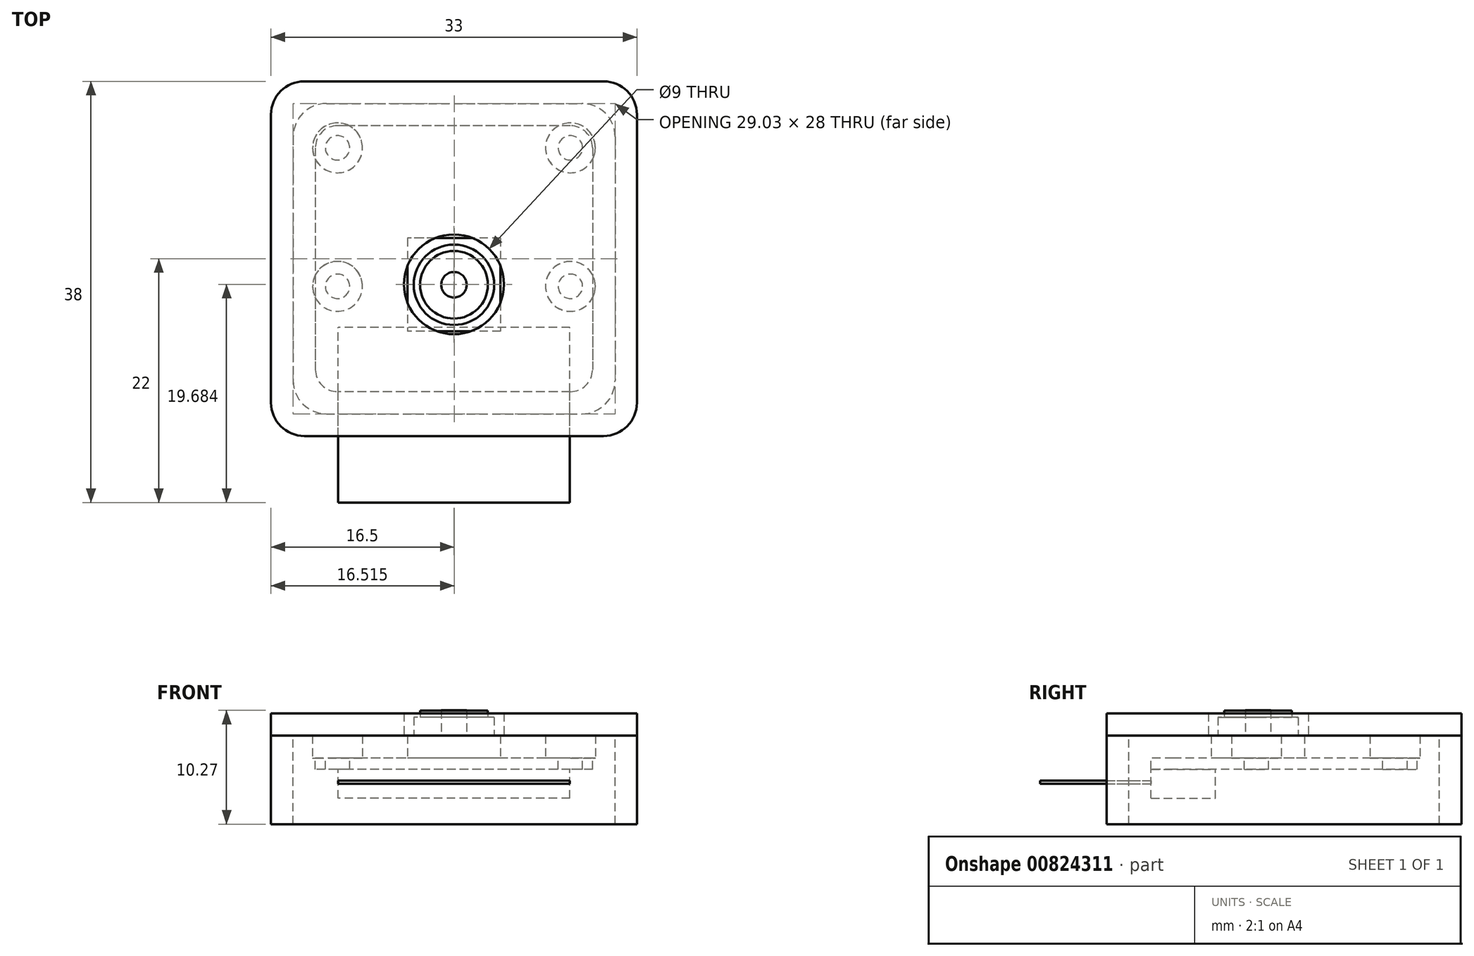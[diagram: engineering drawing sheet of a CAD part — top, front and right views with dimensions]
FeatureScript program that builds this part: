
annotation { "Feature Type Name" : "Feature", "Feature Type Description" : "" }
export const myFeature = defineFeature(function(context is Context, id is Id, definition is map)
    precondition{}
    {
        {
            var Q0;
            Q0=qCreatedBy(makeId("Top.planeOp"),FACE);
            var sketch = newSketch(context, id + "F0", { "sketchPlane" : qUnion([Q0])});
            skLineSegment(sketch, "E0.bottom", {"start": v(10.5, 12) * mm, "end": v(-10.5, 12) * mm});
            skLineSegment(sketch, "E0.top", {"start": v(10.5, -12) * mm, "end": v(-10.5, -12) * mm});
            skLineSegment(sketch, "E0.left", {"start": v(12.5, 10) * mm, "end": v(12.5, -10) * mm});
            skLineSegment(sketch, "E0.right", {"start": v(-12.5, 10) * mm, "end": v(-12.5, -10) * mm});
            skPoint(sketch, "E0.middle", {"position": v(0, 0) * mm});
            skPoint(sketch, "E1.visualSharp", {"position": v(-12.5, 12) * mm});
            skArc(sketch, "E1.filletArc", {"start": v(-10.5, 12) * mm, "mid": v(-11.91, 11.41) * mm, "end": v(-12.5, 10) * mm});
            skPoint(sketch, "E2.visualSharp", {"position": v(12.5, 12) * mm});
            skArc(sketch, "E2.filletArc", {"start": v(12.5, 10) * mm, "mid": v(11.91, 11.41) * mm, "end": v(10.5, 12) * mm});
            skPoint(sketch, "E3.visualSharp", {"position": v(12.5, -12) * mm});
            skArc(sketch, "E3.filletArc", {"start": v(10.5, -12) * mm, "mid": v(11.91, -11.41) * mm, "end": v(12.5, -10) * mm});
            skPoint(sketch, "E4.visualSharp", {"position": v(-12.5, -12) * mm});
            skArc(sketch, "E4.filletArc", {"start": v(-12.5, -10) * mm, "mid": v(-11.91, -11.41) * mm, "end": v(-10.5, -12) * mm});
            skSolve(sketch);
        }
        {
            var Q0;
            Q0=makeQuery(id+"F0.imprint","IMPRINT",FACE,{"disambiguationData":[TD([[makeQuery(id+"F0.imprint","IMPRINT",EDGE,{"derivedFrom":sQuery(id+"F0.wireOp",EDGE,"E0.bottom")}),1.0]])]});
            extrude(context, id + "F1", {"entities" : qUnion([Q0]), "oppositeDirection" : true, "depth" : 1 * mm});
        }
        {
            var Q0;
            Q0=makeQuery(id+"F1.opExtrude","CAP_FACE",FACE,{"disambiguationData":[OSD([sQuery(id+"F0.wireOp",EDGE,"E0.bottom"),sQuery(id+"F0.wireOp",EDGE,"E0.top"),sQuery(id+"F0.wireOp",EDGE,"E0.left"),sQuery(id+"F0.wireOp",EDGE,"E0.right"),sQuery(id+"F0.wireOp",EDGE,"E1.filletArc"),sQuery(id+"F0.wireOp",EDGE,"E2.filletArc"),sQuery(id+"F0.wireOp",EDGE,"E3.filletArc"),sQuery(id+"F0.wireOp",EDGE,"E4.filletArc")])],"isStart":true});
            var sketch = newSketch(context, id + "F2", { "sketchPlane" : qUnion([Q0])});
            skCircle(sketch, "E5", {"center": v(-10.5, 10) * mm, "radius": 1.1 * mm});
            skCircle(sketch, "E6", {"center": v(-10.5, -2.5) * mm, "radius": 1.1 * mm});
            skCircle(sketch, "E7.MirrorC", {"center": v(10.5, -2.5) * mm, "radius": 1.1 * mm});
            skCircle(sketch, "E8.MirrorC", {"center": v(10.5, 10) * mm, "radius": 1.1 * mm});
            skSolve(sketch);
        }
        {
            var Q0;
            Q0=qSketchRegion(id+"F2",true);
            extrude(context, id + "F3", {"entities" : qUnion([Q0]), "operationType" : NewBodyOperationType.REMOVE, "endBound" : BoundingType.UP_TO_NEXT, "oppositeDirection" : true, "depth" : 25 * mm});
        }
        {
            var Q0;
            Q0=makeQuery(id+"F1.opExtrude","CAP_FACE",FACE,{"disambiguationData":[OSD([sQuery(id+"F0.wireOp",EDGE,"E0.bottom"),sQuery(id+"F0.wireOp",EDGE,"E0.top"),sQuery(id+"F0.wireOp",EDGE,"E0.left"),sQuery(id+"F0.wireOp",EDGE,"E0.right"),sQuery(id+"F0.wireOp",EDGE,"E1.filletArc"),sQuery(id+"F0.wireOp",EDGE,"E2.filletArc"),sQuery(id+"F0.wireOp",EDGE,"E3.filletArc"),sQuery(id+"F0.wireOp",EDGE,"E4.filletArc")])],"isStart":true});
            var sketch = newSketch(context, id + "F4", { "sketchPlane" : qUnion([Q0])});
            skLineSegment(sketch, "E9.bottom", {"start": v(4.2, 1.85) * mm, "end": v(-4.2, 1.85) * mm});
            skLineSegment(sketch, "E9.top", {"start": v(4.2, -6.56) * mm, "end": v(-4.2, -6.56) * mm});
            skLineSegment(sketch, "E9.left", {"start": v(4.2, 1.85) * mm, "end": v(4.2, -6.56) * mm});
            skLineSegment(sketch, "E9.right", {"start": v(-4.2, 1.85) * mm, "end": v(-4.2, -6.56) * mm});
            skPoint(sketch, "E9.middle", {"position": v(0, -2.36) * mm});
            skSolve(sketch);
        }
        {
            var Q0;
            Q0=qSketchRegion(id+"F4",true);
            extrude(context, id + "F5", {"entities" : qUnion([Q0]), "depth" : 2.05 * mm});
        }
        {
            var Q0;
            Q0=makeQuery(id+"F5.opExtrude","CAP_FACE",FACE,{"disambiguationData":[OSD([sQuery(id+"F4.wireOp",EDGE,"E9.bottom"),sQuery(id+"F4.wireOp",EDGE,"E9.top"),sQuery(id+"F4.wireOp",EDGE,"E9.left"),sQuery(id+"F4.wireOp",EDGE,"E9.right")])],"isStart":false});
            var sketch = newSketch(context, id + "F6", { "sketchPlane" : qUnion([Q0])});
            skCircle(sketch, "E10", {"center": v(0, -2.36) * mm, "radius": 3.62 * mm});
            skLineSegment(sketch, "E11", {"start": v(0, 1.85) * mm, "end": v(0, -6.56) * mm, "construction": true});
            skLineSegment(sketch, "E12", {"start": v(-4.2, -2.36) * mm, "end": v(4.2, -2.36) * mm, "construction": true});
            skCircle(sketch, "E13", {"center": v(0, -2.36) * mm, "radius": 3.05 * mm});
            skCircle(sketch, "E14", {"center": v(0, -2.36) * mm, "radius": 1.15 * mm});
            skSolve(sketch);
        }
        {
            var Q0;
            Q0=qSketchRegion(id+"F6",true);
            var Q1;
            Q1=makeQuery(id+"F6.imprint","IMPRINT",FACE,{"disambiguationData":[TD([[makeQuery(id+"F6.imprint","IMPRINT",EDGE,{"derivedFrom":sQuery(id+"F6.wireOp",EDGE,"E13")}),1.0]])]});
            var Q2;
            Q2=makeQuery(id+"F6.imprint","IMPRINT",FACE,{"disambiguationData":[TD([[makeQuery(id+"F6.imprint","IMPRINT",EDGE,{"derivedFrom":sQuery(id+"F6.wireOp",EDGE,"E14")}),1.0]])]});
            extrude(context, id + "F7", {"entities" : qUnion([Q0, Q1, Q2]), "operationType" : NewBodyOperationType.ADD, "depth" : 1.65 * mm});
        }
        {
            var Q0;
            Q0=makeQuery(id+"F6.imprint","IMPRINT",FACE,{"disambiguationData":[TD([[makeQuery(id+"F6.imprint","IMPRINT",EDGE,{"derivedFrom":sQuery(id+"F6.wireOp",EDGE,"E13")}),1.0]])]});
            var Q1;
            Q1=makeQuery(id+"F6.imprint","IMPRINT",FACE,{"disambiguationData":[TD([[makeQuery(id+"F6.imprint","IMPRINT",EDGE,{"derivedFrom":sQuery(id+"F6.wireOp",EDGE,"E14")}),1.0]])]});
            extrude(context, id + "F8", {"entities" : qUnion([Q0, Q1]), "operationType" : NewBodyOperationType.ADD, "depth" : 2.25 * mm});
        }
        {
            var Q0;
            Q0=makeQuery(id+"F6.imprint","IMPRINT",FACE,{"disambiguationData":[TD([[makeQuery(id+"F6.imprint","IMPRINT",EDGE,{"derivedFrom":sQuery(id+"F6.wireOp",EDGE,"E14")}),1.0]])]});
            extrude(context, id + "F9", {"entities" : qUnion([Q0]), "depth" : 2.27 * mm});
        }
        {
            var Q0;
            Q0=makeQuery(id+"F1.opExtrude","CAP_FACE",FACE,{"disambiguationData":[OSD([sQuery(id+"F0.wireOp",EDGE,"E0.bottom"),sQuery(id+"F0.wireOp",EDGE,"E0.top"),sQuery(id+"F0.wireOp",EDGE,"E0.left"),sQuery(id+"F0.wireOp",EDGE,"E0.right"),sQuery(id+"F0.wireOp",EDGE,"E1.filletArc"),sQuery(id+"F0.wireOp",EDGE,"E2.filletArc"),sQuery(id+"F0.wireOp",EDGE,"E3.filletArc"),sQuery(id+"F0.wireOp",EDGE,"E4.filletArc")])],"isStart":false});
            var sketch = newSketch(context, id + "F10", { "sketchPlane" : qUnion([Q0])});
            skLineSegment(sketch, "E15.bottom", {"start": v(10.45, 12) * mm, "end": v(-10.45, 12) * mm});
            skLineSegment(sketch, "E15.top", {"start": v(10.45, 6.2) * mm, "end": v(-10.45, 6.2) * mm});
            skLineSegment(sketch, "E15.left", {"start": v(10.45, 12) * mm, "end": v(10.45, 6.2) * mm});
            skLineSegment(sketch, "E15.right", {"start": v(-10.45, 12) * mm, "end": v(-10.45, 6.2) * mm});
            skPoint(sketch, "E15.middle", {"position": v(0, 9.1) * mm});
            skSolve(sketch);
        }
        {
            var Q0;
            Q0=qSketchRegion(id+"F10",true);
            extrude(context, id + "F11", {"entities" : qUnion([Q0]), "depth" : 2.62 * mm});
        }
        {
            var Q0;
            Q0=makeQuery(id+"F11.boolean.opBoolean","MERGE",FACE,{"derivedFrom":[makeQuery(id+"F1.opExtrude","SWEPT_FACE",FACE,{"disambiguationData":[OSD([sQuery(id+"F0.wireOp",EDGE,"E0.top")])]}),makeQuery(id+"F11.opExtrude","SWEPT_FACE",FACE,{"disambiguationData":[OSD([sQuery(id+"F10.wireOp",EDGE,"E15.bottom")])]})]});
            var sketch = newSketch(context, id + "F12", { "sketchPlane" : qUnion([Q0])});
            skLineSegment(sketch, "E16.bottom", {"start": v(-10.45, -2) * mm, "end": v(10.45, -2) * mm});
            skLineSegment(sketch, "E16.top", {"start": v(-10.45, -2.31) * mm, "end": v(10.45, -2.31) * mm});
            skLineSegment(sketch, "E16.left", {"start": v(-10.45, -2) * mm, "end": v(-10.45, -2.31) * mm});
            skLineSegment(sketch, "E16.right", {"start": v(10.45, -2) * mm, "end": v(10.45, -2.31) * mm});
            skSolve(sketch);
        }
        {
            var Q0;
            Q0=qSketchRegion(id+"F12",true);
            extrude(context, id + "F13", {"entities" : qUnion([Q0]), "depth" : 10 * mm});
        }
        {
            var Q0;
            Q0=makeQuery(id+"F1.opExtrude","CAP_FACE",FACE,{"disambiguationData":[OSD([sQuery(id+"F0.wireOp",EDGE,"E0.bottom"),sQuery(id+"F0.wireOp",EDGE,"E0.top"),sQuery(id+"F0.wireOp",EDGE,"E0.left"),sQuery(id+"F0.wireOp",EDGE,"E0.right"),sQuery(id+"F0.wireOp",EDGE,"E1.filletArc"),sQuery(id+"F0.wireOp",EDGE,"E2.filletArc"),sQuery(id+"F0.wireOp",EDGE,"E3.filletArc"),sQuery(id+"F0.wireOp",EDGE,"E4.filletArc")])],"isStart":true});
            var sketch = newSketch(context, id + "F14", { "sketchPlane" : qUnion([Q0])});
            skCircle(sketch, "E17", {"center": v(-10.5, 10) * mm, "radius": 2.25 * mm});
            skCircle(sketch, "E18", {"center": v(10.5, 10) * mm, "radius": 2.25 * mm});
            skCircle(sketch, "E19", {"center": v(10.5, -2.5) * mm, "radius": 2.25 * mm});
            skCircle(sketch, "E20", {"center": v(-10.5, -2.5) * mm, "radius": 2.25 * mm});
            skSolve(sketch);
        }
        {
            var Q0;
            Q0 = qSketchRegion(id + "F14", true);
            var Q1;
            Q1=makeQuery(id+"F5.opExtrude","CAP_FACE",FACE,{"disambiguationData":[OSD([sQuery(id+"F4.wireOp",EDGE,"E9.bottom"),sQuery(id+"F4.wireOp",EDGE,"E9.top"),sQuery(id+"F4.wireOp",EDGE,"E9.left"),sQuery(id+"F4.wireOp",EDGE,"E9.right")])],"isStart":false});
            extrude(context, id + "F15", {"entities" : qUnion([Q0]), "operationType" : NewBodyOperationType.ADD, "endBound" : BoundingType.UP_TO_SURFACE, "depth" : 25 * mm, "endBoundEntityFace" : qUnion([Q1]), "offsetDistance" : 25 * mm});
        }
        {
            var Q0;
            Q0=makeQuery(id+"F15.opExtrude","CAP_FACE",FACE,{"disambiguationData":[OSD([sQuery(id+"F14.wireOp",EDGE,"E20")])],"isStart":false});
            var sketch = newSketch(context, id + "F16", { "sketchPlane" : qUnion([Q0])});
            skLineSegment(sketch, "E21.0", {"start": v(13.5, 16) * mm, "end": v(-13.5, 16) * mm});
            skLineSegment(sketch, "E22.0", {"start": v(-16.5, 13) * mm, "end": v(-16.5, -13) * mm});
            skLineSegment(sketch, "E23.0", {"start": v(16.5, 13) * mm, "end": v(16.5, -13) * mm});
            skLineSegment(sketch, "E24.0", {"start": v(13.5, -16) * mm, "end": v(-13.5, -16) * mm});
            skPoint(sketch, "E25.visualSharp", {"position": v(-16.5, 16) * mm});
            skArc(sketch, "E25.filletArc", {"start": v(-13.5, 16) * mm, "mid": v(-15.62, 15.12) * mm, "end": v(-16.5, 13) * mm});
            skPoint(sketch, "E26.visualSharp", {"position": v(-16.5, -16) * mm});
            skArc(sketch, "E26.filletArc", {"start": v(-16.5, -13) * mm, "mid": v(-15.62, -15.12) * mm, "end": v(-13.5, -16) * mm});
            skPoint(sketch, "E27.visualSharp", {"position": v(16.5, -16) * mm});
            skArc(sketch, "E27.filletArc", {"start": v(13.5, -16) * mm, "mid": v(15.62, -15.12) * mm, "end": v(16.5, -13) * mm});
            skPoint(sketch, "E28.visualSharp", {"position": v(16.5, 16) * mm});
            skArc(sketch, "E28.filletArc", {"start": v(16.5, 13) * mm, "mid": v(15.62, 15.12) * mm, "end": v(13.5, 16) * mm});
            skCircle(sketch, "E29", {"center": v(0, -2.32) * mm, "radius": 4.5 * mm});
            skSolve(sketch);
        }
        {
            var Q0;
            Q0 = qSketchRegion(id + "F16", true);
            extrude(context, id + "F17", {"entities" : qUnion([Q0]), "depth" : 2 * mm, "offsetDistance" : 25 * mm});
        }
        {
            var Q0;
            Q0=makeQuery(id+"F17.opExtrude","CAP_FACE",FACE,{"disambiguationData":[OSD([sQuery(id+"F16.wireOp",EDGE,"E21.0"),sQuery(id+"F16.wireOp",EDGE,"E22.0"),sQuery(id+"F16.wireOp",EDGE,"E23.0"),sQuery(id+"F16.wireOp",EDGE,"E24.0"),sQuery(id+"F16.wireOp",EDGE,"E25.filletArc"),sQuery(id+"F16.wireOp",EDGE,"E26.filletArc"),sQuery(id+"F16.wireOp",EDGE,"E27.filletArc"),sQuery(id+"F16.wireOp",EDGE,"E28.filletArc"),sQuery(id+"F16.wireOp",EDGE,"E29")])],"isStart":true});
            var sketch = newSketch(context, id + "F18", { "sketchPlane" : qUnion([Q0])});
            skLineSegment(sketch, "E30.bottom", {"start": v(-13.5, -16) * mm, "end": v(13.53, -16) * mm});
            skLineSegment(sketch, "E30.top", {"start": v(-13.5, 16) * mm, "end": v(13.53, 16) * mm});
            skLineSegment(sketch, "E30.left", {"start": v(-16.5, -13) * mm, "end": v(-16.5, 13) * mm});
            skLineSegment(sketch, "E30.right", {"start": v(16.53, -13) * mm, "end": v(16.53, 13) * mm});
            skPoint(sketch, "E31.visualSharp", {"position": v(-16.5, 16) * mm});
            skArc(sketch, "E31.filletArc", {"start": v(-13.5, 16) * mm, "mid": v(-15.62, 15.12) * mm, "end": v(-16.5, 13) * mm});
            skPoint(sketch, "E32.visualSharp", {"position": v(16.53, 16) * mm});
            skArc(sketch, "E32.filletArc", {"start": v(16.53, 13) * mm, "mid": v(15.65, 15.12) * mm, "end": v(13.53, 16) * mm});
            skPoint(sketch, "E33.visualSharp", {"position": v(16.53, -16) * mm});
            skArc(sketch, "E33.filletArc", {"start": v(13.53, -16) * mm, "mid": v(15.65, -15.12) * mm, "end": v(16.53, -13) * mm});
            skPoint(sketch, "E34.visualSharp", {"position": v(-16.5, -16) * mm});
            skArc(sketch, "E34.filletArc", {"start": v(-16.5, -13) * mm, "mid": v(-15.62, -15.12) * mm, "end": v(-13.5, -16) * mm});
            skLineSegment(sketch, "E35.0", {"start": v(-11.5, -14) * mm, "end": v(11.53, -14) * mm});
            skLineSegment(sketch, "E36.0", {"start": v(14.53, -11) * mm, "end": v(14.53, 11) * mm});
            skLineSegment(sketch, "E37.0", {"start": v(-11.5, 14) * mm, "end": v(11.53, 14) * mm});
            skLineSegment(sketch, "E38.0", {"start": v(-14.5, -11) * mm, "end": v(-14.5, 11) * mm});
            skArc(sketch, "E39.filletArc", {"start": v(-11.5, 14) * mm, "mid": v(-13.62, 13.12) * mm, "end": v(-14.5, 11) * mm});
            skArc(sketch, "E40.filletArc", {"start": v(14.53, 11) * mm, "mid": v(13.65, 13.12) * mm, "end": v(11.53, 14) * mm});
            skArc(sketch, "E41.filletArc", {"start": v(11.53, -14) * mm, "mid": v(13.65, -13.12) * mm, "end": v(14.53, -11) * mm});
            skArc(sketch, "E42.filletArc", {"start": v(-14.5, -11) * mm, "mid": v(-13.62, -13.12) * mm, "end": v(-11.5, -14) * mm});
            skSolve(sketch);
        }
        {
            var Q0;
            Q0=makeQuery(id+"F18.imprint","IMPRINT",FACE,{"disambiguationData":[TD([[makeQuery(id+"F18.imprint","IMPRINT",EDGE,{"derivedFrom":sQuery(id+"F18.wireOp",EDGE,"E30.left")}),-1.0]])]});
            extrude(context, id + "F19", {"entities" : qUnion([Q0]), "depth" : 8 * mm, "offsetDistance" : 25 * mm});
        }
    });
